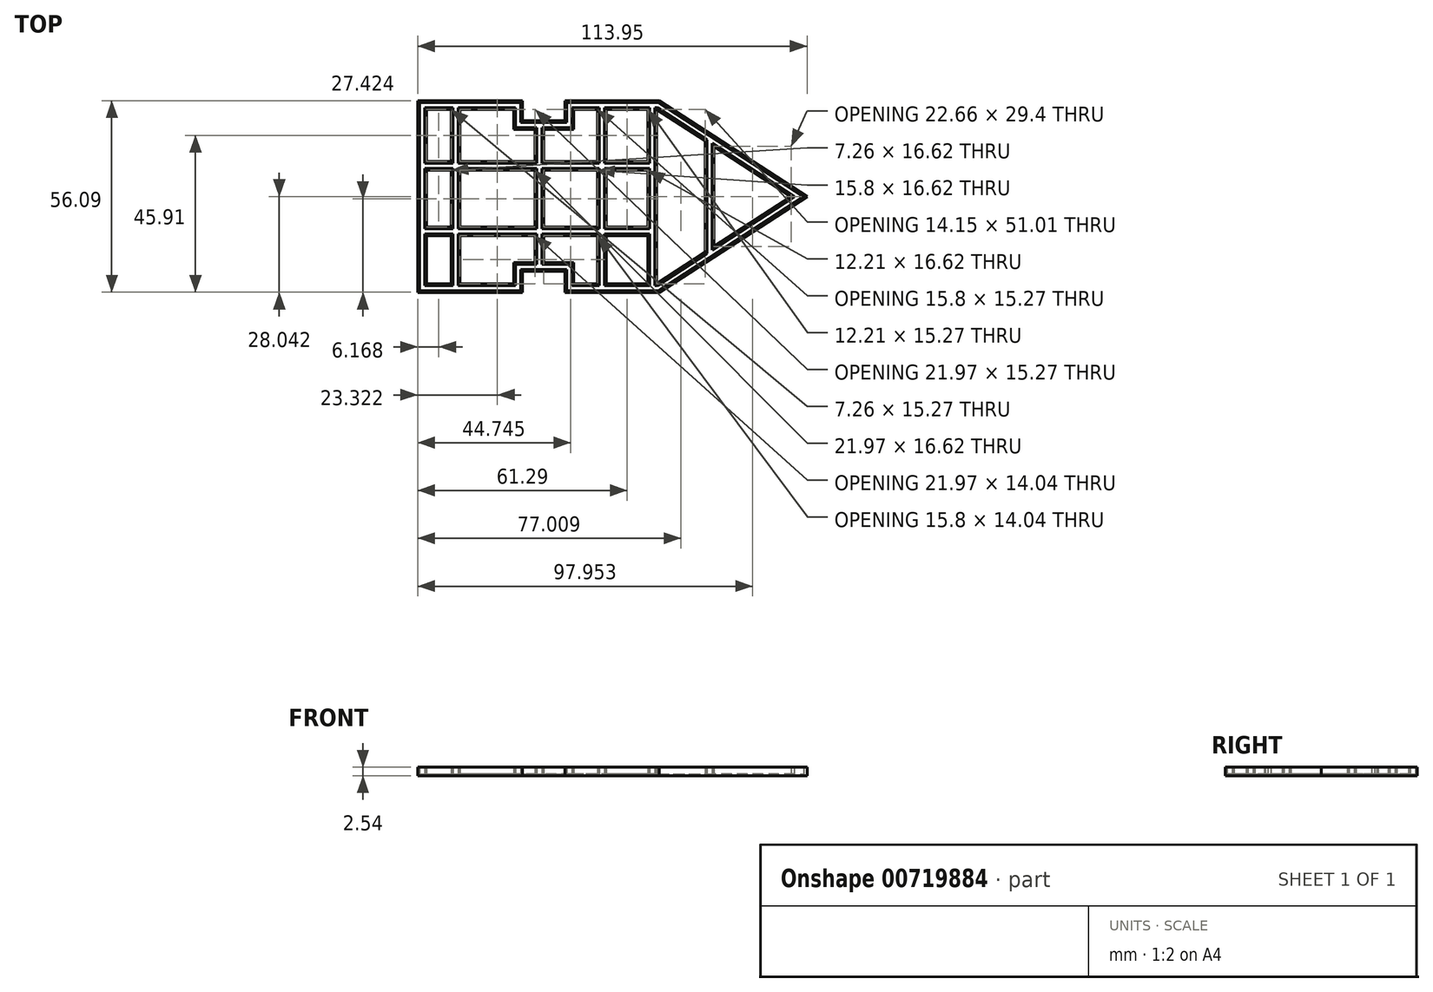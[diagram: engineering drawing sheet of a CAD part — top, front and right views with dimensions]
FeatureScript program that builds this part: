
annotation { "Feature Type Name" : "Feature", "Feature Type Description" : "" }
export const myFeature = defineFeature(function(context is Context, id is Id, definition is map)
    precondition{}
    {
        {
            var Q0;
            Q0=qCreatedBy(makeId("Top.planeOp"),FACE);
            var sketch = newSketch(context, id + "F0", { "sketchPlane" : qUnion([Q0])});
            skLineSegment(sketch, "E0", {"start": v(-89.06, 60.59) * mm, "end": v(-81.8, 60.59) * mm});
            skLineSegment(sketch, "E1", {"start": v(-63.54, 60.59) * mm, "end": v(-63.54, 54.68) * mm});
            skLineSegment(sketch, "E2", {"start": v(-63.54, 54.68) * mm, "end": v(-57.3, 54.68) * mm});
            skLineSegment(sketch, "E3", {"start": v(-45.97, 54.68) * mm, "end": v(-45.97, 60.59) * mm});
            skLineSegment(sketch, "E4", {"start": v(-45.97, 60.59) * mm, "end": v(-38.96, 60.59) * mm});
            skLineSegment(sketch, "E5", {"start": v(-21.64, 9.58) * mm, "end": v(-21.66, 9.58) * mm});
            skLineSegment(sketch, "E6", {"start": v(-45.97, 9.58) * mm, "end": v(-45.97, 15.67) * mm});
            skLineSegment(sketch, "E7", {"start": v(-45.97, 15.67) * mm, "end": v(-54.75, 15.67) * mm});
            skLineSegment(sketch, "E8", {"start": v(-63.54, 15.67) * mm, "end": v(-63.54, 9.58) * mm});
            skLineSegment(sketch, "E9", {"start": v(-63.54, 9.58) * mm, "end": v(-79.26, 9.58) * mm});
            skLineSegment(sketch, "E10", {"start": v(-89.06, 9.58) * mm, "end": v(-89.06, 23.62) * mm});
            skLineSegment(sketch, "E11", {"start": v(-21.64, 9.58) * mm, "end": v(-7.52, 18.73) * mm});
            skLineSegment(sketch, "E12", {"start": v(17.68, 35.08) * mm, "end": v(-4.98, 49.78) * mm});
            skLineSegment(sketch, "E13", {"start": v(-4.98, 49.78) * mm, "end": v(-4.98, 20.38) * mm});
            skLineSegment(sketch, "E14", {"start": v(-89.06, 26.16) * mm, "end": v(-81.8, 26.16) * mm});
            skLineSegment(sketch, "E15", {"start": v(-21.64, 42.77) * mm, "end": v(-21.66, 42.77) * mm});
            skLineSegment(sketch, "E16", {"start": v(-79.26, 60.59) * mm, "end": v(-79.26, 45.31) * mm});
            skLineSegment(sketch, "E17", {"start": v(-54.75, 54.68) * mm, "end": v(-54.75, 45.31) * mm});
            skLineSegment(sketch, "E18", {"start": v(-36.42, 60.59) * mm, "end": v(-36.42, 45.31) * mm});
            skLineSegment(sketch, "E19.0", {"start": v(-89.06, 23.62) * mm, "end": v(-81.8, 23.62) * mm});
            skLineSegment(sketch, "E20.0", {"start": v(-21.64, 45.31) * mm, "end": v(-21.66, 45.31) * mm});
            skLineSegment(sketch, "E21.0", {"start": v(-57.3, 54.68) * mm, "end": v(-57.3, 45.31) * mm});
            skLineSegment(sketch, "E22.0", {"start": v(-38.96, 60.59) * mm, "end": v(-38.96, 45.31) * mm});
            skLineSegment(sketch, "E23.0", {"start": v(-21.66, 60.59) * mm, "end": v(-21.66, 9.58) * mm});
            skLineSegment(sketch, "E24.0", {"start": v(-81.8, 60.59) * mm, "end": v(-81.8, 45.31) * mm});
            skLineSegment(sketch, "E25.0", {"start": v(-24.2, 60.59) * mm, "end": v(-24.2, 45.31) * mm});
            skLineSegment(sketch, "E26.0", {"start": v(-7.52, 51.43) * mm, "end": v(-7.52, 18.73) * mm});
            skLineSegment(sketch, "E27.0", {"start": v(-20.88, 7.04) * mm, "end": v(-48.51, 7.04) * mm});
            skLineSegment(sketch, "E27.1", {"start": v(-48.51, 7.04) * mm, "end": v(-48.51, 13.13) * mm});
            skLineSegment(sketch, "E27.2", {"start": v(-61, 57.22) * mm, "end": v(-48.51, 57.22) * mm});
            skLineSegment(sketch, "E27.3", {"start": v(-48.51, 57.22) * mm, "end": v(-48.51, 63.13) * mm});
            skLineSegment(sketch, "E27.4", {"start": v(-48.51, 63.13) * mm, "end": v(-20.88, 63.13) * mm});
            skLineSegment(sketch, "E27.5", {"start": v(22.35, 35.08) * mm, "end": v(-20.88, 63.13) * mm});
            skLineSegment(sketch, "E27.6", {"start": v(-61, 63.13) * mm, "end": v(-61, 57.22) * mm});
            skLineSegment(sketch, "E27.7", {"start": v(-91.6, 63.13) * mm, "end": v(-61, 63.13) * mm});
            skLineSegment(sketch, "E27.8", {"start": v(-20.88, 7.04) * mm, "end": v(22.35, 35.08) * mm});
            skLineSegment(sketch, "E27.9", {"start": v(-91.6, 7.04) * mm, "end": v(-91.6, 63.13) * mm});
            skLineSegment(sketch, "E27.10", {"start": v(-61, 7.04) * mm, "end": v(-91.6, 7.04) * mm});
            skLineSegment(sketch, "E27.11", {"start": v(-61, 13.13) * mm, "end": v(-61, 7.04) * mm});
            skLineSegment(sketch, "E27.12", {"start": v(-48.51, 13.13) * mm, "end": v(-61, 13.13) * mm});
            skLineSegment(sketch, "E28.trimOffspring", {"start": v(-38.96, 9.58) * mm, "end": v(-45.97, 9.58) * mm});
            skLineSegment(sketch, "E29.trimOffspring", {"start": v(-24.2, 9.58) * mm, "end": v(-36.42, 9.58) * mm});
            skLineSegment(sketch, "E30.trimOffspring", {"start": v(-21.66, 23.62) * mm, "end": v(-21.64, 23.62) * mm});
            skLineSegment(sketch, "E31.trimOffspring", {"start": v(-21.66, 26.16) * mm, "end": v(-21.64, 26.16) * mm});
            skLineSegment(sketch, "E32.trimOffspring", {"start": v(-24.2, 23.62) * mm, "end": v(-24.2, 9.58) * mm});
            skLineSegment(sketch, "E33.trimOffspring", {"start": v(-36.42, 23.62) * mm, "end": v(-36.42, 9.58) * mm});
            skLineSegment(sketch, "E34.trimOffspring", {"start": v(-38.96, 23.62) * mm, "end": v(-38.96, 9.58) * mm});
            skLineSegment(sketch, "E35.trimOffspring", {"start": v(-36.42, 23.62) * mm, "end": v(-24.2, 23.62) * mm});
            skLineSegment(sketch, "E36.trimOffspring", {"start": v(-36.42, 26.16) * mm, "end": v(-24.2, 26.16) * mm});
            skLineSegment(sketch, "E37.trimOffspring", {"start": v(-24.2, 42.77) * mm, "end": v(-36.42, 42.77) * mm});
            skLineSegment(sketch, "E38.trimOffspring", {"start": v(-24.2, 42.77) * mm, "end": v(-24.2, 26.16) * mm});
            skLineSegment(sketch, "E39.trimOffspring", {"start": v(-24.2, 45.31) * mm, "end": v(-36.42, 45.31) * mm});
            skLineSegment(sketch, "E40.trimOffspring", {"start": v(-54.75, 42.77) * mm, "end": v(-54.75, 26.16) * mm});
            skLineSegment(sketch, "E41.trimOffspring", {"start": v(-57.3, 42.77) * mm, "end": v(-57.3, 26.16) * mm});
            skLineSegment(sketch, "E42.trimOffspring", {"start": v(-57.3, 23.62) * mm, "end": v(-57.3, 15.67) * mm});
            skLineSegment(sketch, "E43.trimOffspring", {"start": v(-54.75, 26.16) * mm, "end": v(-38.96, 26.16) * mm});
            skLineSegment(sketch, "E44.trimOffspring", {"start": v(-54.75, 23.62) * mm, "end": v(-38.96, 23.62) * mm});
            skLineSegment(sketch, "E45.trimOffspring", {"start": v(-54.75, 23.62) * mm, "end": v(-54.75, 15.67) * mm});
            skLineSegment(sketch, "E46.trimOffspring", {"start": v(-4.98, 20.38) * mm, "end": v(17.68, 35.08) * mm});
            skLineSegment(sketch, "E47.trimOffspring", {"start": v(-7.52, 51.43) * mm, "end": v(-21.64, 60.59) * mm});
            skLineSegment(sketch, "E48.trimOffspring", {"start": v(-57.3, 15.67) * mm, "end": v(-63.54, 15.67) * mm});
            skLineSegment(sketch, "E49.trimOffspring", {"start": v(-54.75, 54.68) * mm, "end": v(-45.97, 54.68) * mm});
            skLineSegment(sketch, "E50.trimOffspring", {"start": v(-57.3, 42.77) * mm, "end": v(-79.26, 42.77) * mm});
            skLineSegment(sketch, "E51.trimOffspring", {"start": v(-57.3, 45.31) * mm, "end": v(-79.26, 45.31) * mm});
            skLineSegment(sketch, "E52.trimOffspring", {"start": v(-81.8, 42.77) * mm, "end": v(-81.8, 26.16) * mm});
            skLineSegment(sketch, "E53.trimOffspring", {"start": v(-81.8, 45.31) * mm, "end": v(-89.06, 45.31) * mm});
            skLineSegment(sketch, "E54.trimOffspring", {"start": v(-81.8, 42.77) * mm, "end": v(-89.06, 42.77) * mm});
            skLineSegment(sketch, "E55.trimOffspring", {"start": v(-79.26, 42.77) * mm, "end": v(-79.26, 26.16) * mm});
            skLineSegment(sketch, "E56.trimOffspring", {"start": v(-79.26, 23.62) * mm, "end": v(-79.26, 9.58) * mm});
            skLineSegment(sketch, "E57.trimOffspring", {"start": v(-81.8, 23.62) * mm, "end": v(-81.8, 9.58) * mm});
            skLineSegment(sketch, "E58.trimOffspring", {"start": v(-79.26, 26.16) * mm, "end": v(-57.3, 26.16) * mm});
            skLineSegment(sketch, "E59.trimOffspring", {"start": v(-79.26, 23.62) * mm, "end": v(-57.3, 23.62) * mm});
            skLineSegment(sketch, "E60.trimOffspring", {"start": v(-89.06, 26.16) * mm, "end": v(-89.06, 42.77) * mm});
            skLineSegment(sketch, "E61.trimOffspring", {"start": v(-89.06, 45.31) * mm, "end": v(-89.06, 60.59) * mm});
            skLineSegment(sketch, "E62.trimOffspring", {"start": v(-79.26, 60.59) * mm, "end": v(-63.54, 60.59) * mm});
            skLineSegment(sketch, "E63.trimOffspring", {"start": v(-81.8, 9.58) * mm, "end": v(-89.06, 9.58) * mm});
            skLineSegment(sketch, "E64.trimOffspring", {"start": v(-38.96, 45.31) * mm, "end": v(-54.75, 45.31) * mm});
            skLineSegment(sketch, "E65.trimOffspring", {"start": v(-38.96, 42.77) * mm, "end": v(-38.96, 26.16) * mm});
            skLineSegment(sketch, "E66.trimOffspring", {"start": v(-36.42, 42.77) * mm, "end": v(-36.42, 26.16) * mm});
            skLineSegment(sketch, "E67.trimOffspring", {"start": v(-38.96, 42.77) * mm, "end": v(-54.75, 42.77) * mm});
            skLineSegment(sketch, "E68.trimOffspring", {"start": v(-36.42, 60.59) * mm, "end": v(-24.2, 60.59) * mm});
            skLineSegment(sketch, "E69.trimOffspring", {"start": v(-21.66, 60.59) * mm, "end": v(-21.64, 60.59) * mm});
            skSolve(sketch);
        }
        {
            var Q0;
            Q0=makeQuery(id+"F0.imprint","IMPRINT",FACE,{"disambiguationData":[TD([[makeQuery(id+"F0.imprint","IMPRINT",EDGE,{"derivedFrom":sQuery(id+"F0.wireOp",EDGE,"E0")}),1.0]])]});
            extrude(context, id + "F1", {"entities" : qUnion([Q0]), "depth" : 2.54 * mm, "offsetDistance" : 25.4 * mm});
        }
        {
            var Q0;
            Q0=makeQuery(id+"F1.opExtrude","CAP_FACE",FACE,{"disambiguationData":[OSD([sQuery(id+"F0.wireOp",EDGE,"E0"),sQuery(id+"F0.wireOp",EDGE,"E1"),sQuery(id+"F0.wireOp",EDGE,"E2"),sQuery(id+"F0.wireOp",EDGE,"E3"),sQuery(id+"F0.wireOp",EDGE,"E4"),sQuery(id+"F0.wireOp",EDGE,"E5"),sQuery(id+"F0.wireOp",EDGE,"E6"),sQuery(id+"F0.wireOp",EDGE,"E7"),sQuery(id+"F0.wireOp",EDGE,"E8"),sQuery(id+"F0.wireOp",EDGE,"E9"),sQuery(id+"F0.wireOp",EDGE,"E10"),sQuery(id+"F0.wireOp",EDGE,"E11"),sQuery(id+"F0.wireOp",EDGE,"E12"),sQuery(id+"F0.wireOp",EDGE,"E13"),sQuery(id+"F0.wireOp",EDGE,"E14"),sQuery(id+"F0.wireOp",EDGE,"E16"),sQuery(id+"F0.wireOp",EDGE,"E17"),sQuery(id+"F0.wireOp",EDGE,"E18"),sQuery(id+"F0.wireOp",EDGE,"E19.0"),sQuery(id+"F0.wireOp",EDGE,"E21.0"),sQuery(id+"F0.wireOp",EDGE,"E22.0"),sQuery(id+"F0.wireOp",EDGE,"E23.0"),sQuery(id+"F0.wireOp",EDGE,"E24.0"),sQuery(id+"F0.wireOp",EDGE,"E25.0"),sQuery(id+"F0.wireOp",EDGE,"E26.0"),sQuery(id+"F0.wireOp",EDGE,"E27.0"),sQuery(id+"F0.wireOp",EDGE,"E27.1"),sQuery(id+"F0.wireOp",EDGE,"E27.2"),sQuery(id+"F0.wireOp",EDGE,"E27.3"),sQuery(id+"F0.wireOp",EDGE,"E27.4"),sQuery(id+"F0.wireOp",EDGE,"E27.5"),sQuery(id+"F0.wireOp",EDGE,"E27.6"),sQuery(id+"F0.wireOp",EDGE,"E27.7"),sQuery(id+"F0.wireOp",EDGE,"E27.8"),sQuery(id+"F0.wireOp",EDGE,"E27.9"),sQuery(id+"F0.wireOp",EDGE,"E27.10"),sQuery(id+"F0.wireOp",EDGE,"E27.11"),sQuery(id+"F0.wireOp",EDGE,"E27.12"),sQuery(id+"F0.wireOp",EDGE,"E28.trimOffspring"),sQuery(id+"F0.wireOp",EDGE,"E29.trimOffspring"),sQuery(id+"F0.wireOp",EDGE,"E32.trimOffspring"),sQuery(id+"F0.wireOp",EDGE,"E33.trimOffspring"),sQuery(id+"F0.wireOp",EDGE,"E34.trimOffspring"),sQuery(id+"F0.wireOp",EDGE,"E35.trimOffspring"),sQuery(id+"F0.wireOp",EDGE,"E36.trimOffspring"),sQuery(id+"F0.wireOp",EDGE,"E37.trimOffspring"),sQuery(id+"F0.wireOp",EDGE,"E38.trimOffspring"),sQuery(id+"F0.wireOp",EDGE,"E39.trimOffspring"),sQuery(id+"F0.wireOp",EDGE,"E40.trimOffspring"),sQuery(id+"F0.wireOp",EDGE,"E41.trimOffspring"),sQuery(id+"F0.wireOp",EDGE,"E42.trimOffspring"),sQuery(id+"F0.wireOp",EDGE,"E43.trimOffspring"),sQuery(id+"F0.wireOp",EDGE,"E44.trimOffspring"),sQuery(id+"F0.wireOp",EDGE,"E45.trimOffspring"),sQuery(id+"F0.wireOp",EDGE,"E46.trimOffspring"),sQuery(id+"F0.wireOp",EDGE,"E47.trimOffspring"),sQuery(id+"F0.wireOp",EDGE,"E48.trimOffspring"),sQuery(id+"F0.wireOp",EDGE,"E49.trimOffspring"),sQuery(id+"F0.wireOp",EDGE,"E50.trimOffspring"),sQuery(id+"F0.wireOp",EDGE,"E51.trimOffspring"),sQuery(id+"F0.wireOp",EDGE,"E52.trimOffspring"),sQuery(id+"F0.wireOp",EDGE,"E53.trimOffspring"),sQuery(id+"F0.wireOp",EDGE,"E54.trimOffspring"),sQuery(id+"F0.wireOp",EDGE,"E55.trimOffspring"),sQuery(id+"F0.wireOp",EDGE,"E56.trimOffspring"),sQuery(id+"F0.wireOp",EDGE,"E57.trimOffspring"),sQuery(id+"F0.wireOp",EDGE,"E58.trimOffspring"),sQuery(id+"F0.wireOp",EDGE,"E59.trimOffspring"),sQuery(id+"F0.wireOp",EDGE,"E60.trimOffspring"),sQuery(id+"F0.wireOp",EDGE,"E61.trimOffspring"),sQuery(id+"F0.wireOp",EDGE,"E62.trimOffspring"),sQuery(id+"F0.wireOp",EDGE,"E63.trimOffspring"),sQuery(id+"F0.wireOp",EDGE,"E64.trimOffspring"),sQuery(id+"F0.wireOp",EDGE,"E65.trimOffspring"),sQuery(id+"F0.wireOp",EDGE,"E66.trimOffspring"),sQuery(id+"F0.wireOp",EDGE,"E67.trimOffspring"),sQuery(id+"F0.wireOp",EDGE,"E68.trimOffspring"),sQuery(id+"F0.wireOp",EDGE,"E69.trimOffspring")])],"isStart":false});
            shell(context, id + "F2", {"entities" : qUnion([Q0]), "thickness" : 0.5 * mm});
        }
    });
